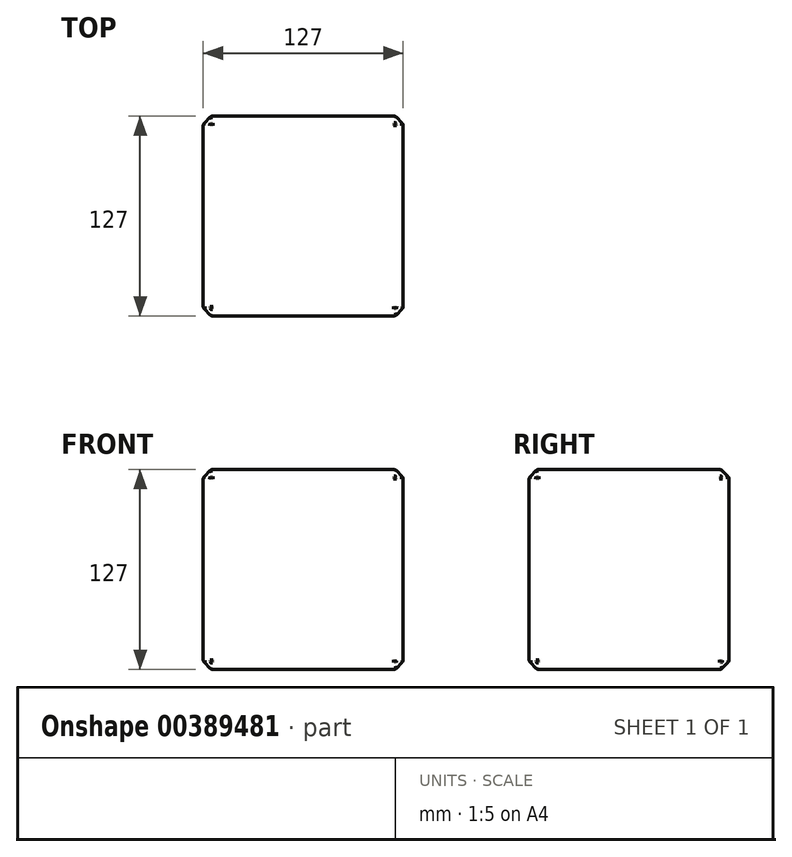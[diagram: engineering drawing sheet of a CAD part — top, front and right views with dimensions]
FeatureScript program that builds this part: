
annotation { "Feature Type Name" : "Feature", "Feature Type Description" : "" }
export const myFeature = defineFeature(function(context is Context, id is Id, definition is map)
    precondition{}
    {
        {
            var Q0;
            Q0=qCreatedBy(makeId("Top.planeOp"),FACE);
            var sketch = newSketch(context, id + "F0", { "sketchPlane" : qUnion([Q0])});
            skLineSegment(sketch, "E0.bottom", {"start": v(63.5, 63.5) * mm, "end": v(-63.5, 63.5) * mm});
            skLineSegment(sketch, "E0.top", {"start": v(63.5, -63.5) * mm, "end": v(-63.5, -63.5) * mm});
            skLineSegment(sketch, "E0.left", {"start": v(63.5, 63.5) * mm, "end": v(63.5, -63.5) * mm});
            skLineSegment(sketch, "E0.right", {"start": v(-63.5, 63.5) * mm, "end": v(-63.5, -63.5) * mm});
            skPoint(sketch, "E0.middle", {"position": v(0, 0) * mm});
            skSolve(sketch);
        }
        {
            var Q0;
            Q0 = qSketchRegion(id + "F0", true);
            extrude(context, id + "F1", {"entities" : qUnion([Q0]), "depth" : 127 * mm});
        }
        {
            var Q0;
            Q0=makeQuery(id+"F1.opExtrude","CAP_EDGE",EDGE,{"disambiguationData":[OSD([sQuery(id+"F0.wireOp",EDGE,"E0.top")])],"isStart":false});
            var Q1;
            Q1=makeQuery(id+"F1.opExtrude","CAP_EDGE",EDGE,{"disambiguationData":[OSD([sQuery(id+"F0.wireOp",EDGE,"E0.left")])],"isStart":false});
            var Q2;
            Q2=makeQuery(id+"F1.opExtrude","SWEPT_EDGE",EDGE,{"disambiguationData":[OSD([sQuery(id+"F0.wireOp",EDGE,"E0.top"),sQuery(id+"F0.wireOp",EDGE,"E0.left")])]});
            var Q3;
            Q3=makeQuery(id+"F1.opExtrude","SWEPT_EDGE",EDGE,{"disambiguationData":[OSD([sQuery(id+"F0.wireOp",EDGE,"E0.bottom"),sQuery(id+"F0.wireOp",EDGE,"E0.left")])]});
            var Q4;
            Q4=makeQuery(id+"F1.opExtrude","CAP_EDGE",EDGE,{"disambiguationData":[OSD([sQuery(id+"F0.wireOp",EDGE,"E0.top")])],"isStart":true});
            var Q5;
            Q5=makeQuery(id+"F1.opExtrude","CAP_EDGE",EDGE,{"disambiguationData":[OSD([sQuery(id+"F0.wireOp",EDGE,"E0.left")])],"isStart":true});
            var Q6;
            Q6=makeQuery(id+"F1.opExtrude","SWEPT_EDGE",EDGE,{"disambiguationData":[OSD([sQuery(id+"F0.wireOp",EDGE,"E0.top"),sQuery(id+"F0.wireOp",EDGE,"E0.right")])]});
            var Q7;
            Q7=makeQuery(id+"F1.opExtrude","CAP_EDGE",EDGE,{"disambiguationData":[OSD([sQuery(id+"F0.wireOp",EDGE,"E0.right")])],"isStart":true});
            var Q8;
            Q8=makeQuery(id+"F1.opExtrude","CAP_EDGE",EDGE,{"disambiguationData":[OSD([sQuery(id+"F0.wireOp",EDGE,"E0.right")])],"isStart":false});
            var Q9;
            Q9=makeQuery(id+"F1.opExtrude","SWEPT_FACE",FACE,{"disambiguationData":[OSD([sQuery(id+"F0.wireOp",EDGE,"E0.bottom")])]});
            chamfer(context, id + "F2", {"entities" : qUnion([Q0, Q1, Q2, Q3, Q4, Q5, Q6, Q7, Q8, Q9]), "width" : 5.08 * mm, "tangentPropagation" : true});
        }
        {
            var Q0;
            {var subQ0=sQuery(id+"F0.wireOp",EDGE,"E0.top");Q0=makeQuery(id+"F2.opChamfer","BLEND_EDGE",EDGE,{"blendedFrom":[makeQuery(id+"F1.opExtrude","SWEPT_EDGE",EDGE,{"disambiguationData":[OSD([subQ0,sQuery(id+"F0.wireOp",EDGE,"E0.left")])]}),makeQuery(id+"F1.opExtrude","SWEPT_FACE",FACE,{"disambiguationData":[OSD([subQ0])]})],"blendedInto":[makeQuery(id+"F1.opExtrude","SWEPT_FACE",FACE,{"disambiguationData":[OSD([subQ0])]})]});}
            var Q1;
            {var subQ0=sQuery(id+"F0.wireOp",EDGE,"E0.left");Q1=makeQuery(id+"F2.opChamfer","BLEND_EDGE",EDGE,{"blendedFrom":[makeQuery(id+"F1.opExtrude","SWEPT_EDGE",EDGE,{"disambiguationData":[OSD([sQuery(id+"F0.wireOp",EDGE,"E0.top"),subQ0])]}),makeQuery(id+"F1.opExtrude","SWEPT_FACE",FACE,{"disambiguationData":[OSD([subQ0])]})],"blendedInto":[makeQuery(id+"F1.opExtrude","SWEPT_FACE",FACE,{"disambiguationData":[OSD([subQ0])]})]});}
            var Q2;
            {var subQ0=sQuery(id+"F0.wireOp",EDGE,"E0.left");var subQ1=sQuery(id+"F0.wireOp",EDGE,"E0.top");Q2=makeQuery(id+"F2.opChamfer","BLEND_EDGE",EDGE,{"blendedFrom":[makeQuery(id+"F1.opExtrude","CAP_VERTEX",VERTEX,{"disambiguationData":[OSD([subQ1,subQ0])],"isStart":false}),makeQuery(id+"F1.opExtrude","SWEPT_EDGE",EDGE,{"disambiguationData":[OSD([subQ1,subQ0])]})],"blendedInto":[]});}
            var Q3;
            {var subQ0=sQuery(id+"F0.wireOp",EDGE,"E0.left");Q3=makeQuery(id+"F2.opChamfer","BLEND_EDGE",EDGE,{"blendedFrom":[makeQuery(id+"F1.opExtrude","CAP_EDGE",EDGE,{"disambiguationData":[OSD([subQ0])],"isStart":false}),makeQuery(id+"F1.opExtrude","SWEPT_FACE",FACE,{"disambiguationData":[OSD([subQ0])]})],"blendedInto":[makeQuery(id+"F1.opExtrude","SWEPT_FACE",FACE,{"disambiguationData":[OSD([subQ0])]})]});}
            var Q4;
            {var subQ0=sQuery(id+"F0.wireOp",EDGE,"E0.left");Q4=makeQuery(id+"F2.opChamfer","BLEND_EDGE",EDGE,{"blendedFrom":[makeQuery(id+"F1.opExtrude","CAP_EDGE",EDGE,{"disambiguationData":[OSD([subQ0])],"isStart":false}),makeQuery(id+"F1.opExtrude","CAP_FACE",FACE,{"disambiguationData":[OSD([sQuery(id+"F0.wireOp",EDGE,"E0.bottom"),sQuery(id+"F0.wireOp",EDGE,"E0.top"),subQ0,sQuery(id+"F0.wireOp",EDGE,"E0.right")])],"isStart":false})],"blendedInto":[makeQuery(id+"F1.opExtrude","CAP_FACE",FACE,{"disambiguationData":[OSD([sQuery(id+"F0.wireOp",EDGE,"E0.bottom"),sQuery(id+"F0.wireOp",EDGE,"E0.top"),subQ0,sQuery(id+"F0.wireOp",EDGE,"E0.right")])],"isStart":false})]});}
            var Q5;
            {var subQ0=sQuery(id+"F0.wireOp",EDGE,"E0.left");Q5=makeQuery(id+"F2.opChamfer","BLEND_EDGE",EDGE,{"blendedFrom":[makeQuery(id+"F1.opExtrude","CAP_VERTEX",VERTEX,{"disambiguationData":[OSD([sQuery(id+"F0.wireOp",EDGE,"E0.top"),subQ0])],"isStart":false}),makeQuery(id+"F1.opExtrude","CAP_EDGE",EDGE,{"disambiguationData":[OSD([subQ0])],"isStart":false})],"blendedInto":[]});}
            var Q6;
            {var subQ0=sQuery(id+"F0.wireOp",EDGE,"E0.top");Q6=makeQuery(id+"F2.opChamfer","BLEND_EDGE",EDGE,{"blendedFrom":[makeQuery(id+"F1.opExtrude","CAP_EDGE",EDGE,{"disambiguationData":[OSD([subQ0])],"isStart":false}),makeQuery(id+"F1.opExtrude","CAP_FACE",FACE,{"disambiguationData":[OSD([sQuery(id+"F0.wireOp",EDGE,"E0.bottom"),subQ0,sQuery(id+"F0.wireOp",EDGE,"E0.left"),sQuery(id+"F0.wireOp",EDGE,"E0.right")])],"isStart":false})],"blendedInto":[makeQuery(id+"F1.opExtrude","CAP_FACE",FACE,{"disambiguationData":[OSD([sQuery(id+"F0.wireOp",EDGE,"E0.bottom"),subQ0,sQuery(id+"F0.wireOp",EDGE,"E0.left"),sQuery(id+"F0.wireOp",EDGE,"E0.right")])],"isStart":false})]});}
            var Q7;
            {var subQ0=sQuery(id+"F0.wireOp",EDGE,"E0.top");Q7=makeQuery(id+"F2.opChamfer","BLEND_EDGE",EDGE,{"blendedFrom":[makeQuery(id+"F1.opExtrude","CAP_EDGE",EDGE,{"disambiguationData":[OSD([subQ0])],"isStart":false}),makeQuery(id+"F1.opExtrude","SWEPT_FACE",FACE,{"disambiguationData":[OSD([subQ0])]})],"blendedInto":[makeQuery(id+"F1.opExtrude","SWEPT_FACE",FACE,{"disambiguationData":[OSD([subQ0])]})]});}
            var Q8;
            {var subQ0=sQuery(id+"F0.wireOp",EDGE,"E0.top");Q8=makeQuery(id+"F2.opChamfer","BLEND_EDGE",EDGE,{"blendedFrom":[makeQuery(id+"F1.opExtrude","CAP_VERTEX",VERTEX,{"disambiguationData":[OSD([subQ0,sQuery(id+"F0.wireOp",EDGE,"E0.left")])],"isStart":false}),makeQuery(id+"F1.opExtrude","CAP_EDGE",EDGE,{"disambiguationData":[OSD([subQ0])],"isStart":false})],"blendedInto":[]});}
            var Q9;
            {var subQ0=sQuery(id+"F0.wireOp",EDGE,"E0.top");Q9=makeQuery(id+"F2.opChamfer","BLEND_EDGE",EDGE,{"blendedFrom":[makeQuery(id+"F1.opExtrude","CAP_VERTEX",VERTEX,{"disambiguationData":[OSD([subQ0,sQuery(id+"F0.wireOp",EDGE,"E0.right")])],"isStart":false}),makeQuery(id+"F1.opExtrude","CAP_EDGE",EDGE,{"disambiguationData":[OSD([subQ0])],"isStart":false})],"blendedInto":[]});}
            var Q10;
            {var subQ0=sQuery(id+"F0.wireOp",EDGE,"E0.right");var subQ1=sQuery(id+"F0.wireOp",EDGE,"E0.top");Q10=makeQuery(id+"F2.opChamfer","BLEND_FACE",FACE,{"disambiguationData":[OSD([subQ1,subQ0]),TDD([makeQuery(id+"F1.opExtrude","SWEPT_EDGE",EDGE,{"disambiguationData":[OSD([subQ1,subQ0])]})])]});}
            var Q11;
            {var subQ0=sQuery(id+"F0.wireOp",EDGE,"E0.right");Q11=makeQuery(id+"F2.opChamfer","BLEND_FACE",FACE,{"disambiguationData":[OSD([subQ0]),TDD([makeQuery(id+"F1.opExtrude","CAP_EDGE",EDGE,{"disambiguationData":[OSD([subQ0])],"isStart":false})])]});}
            var Q12;
            {var subQ0=sQuery(id+"F0.wireOp",EDGE,"E0.top");Q12=makeQuery(id+"F2.opChamfer","BLEND_FACE",FACE,{"disambiguationData":[OSD([subQ0]),TDD([makeQuery(id+"F1.opExtrude","CAP_EDGE",EDGE,{"disambiguationData":[OSD([subQ0])],"isStart":true})])]});}
            var Q13;
            {var subQ0=sQuery(id+"F0.wireOp",EDGE,"E0.right");Q13=makeQuery(id+"F2.opChamfer","BLEND_FACE",FACE,{"disambiguationData":[OSD([subQ0]),TDD([makeQuery(id+"F1.opExtrude","CAP_EDGE",EDGE,{"disambiguationData":[OSD([subQ0])],"isStart":true})])]});}
            var Q14;
            {var subQ0=sQuery(id+"F0.wireOp",EDGE,"E0.left");Q14=makeQuery(id+"F2.opChamfer","BLEND_FACE",FACE,{"disambiguationData":[OSD([subQ0]),TDD([makeQuery(id+"F1.opExtrude","CAP_EDGE",EDGE,{"disambiguationData":[OSD([subQ0])],"isStart":true})])]});}
            var Q15;
            {var subQ0=sQuery(id+"F0.wireOp",EDGE,"E0.bottom");Q15=makeQuery(id+"F2.opChamfer","BLEND_FACE",FACE,{"disambiguationData":[OSD([subQ0]),TDD([makeQuery(id+"F1.opExtrude","CAP_EDGE",EDGE,{"disambiguationData":[OSD([subQ0])],"isStart":true})])]});}
            var Q16;
            {var subQ0=sQuery(id+"F0.wireOp",EDGE,"E0.left");var subQ1=sQuery(id+"F0.wireOp",EDGE,"E0.bottom");Q16=makeQuery(id+"F2.opChamfer","BLEND_FACE",FACE,{"disambiguationData":[OSD([subQ1,subQ0]),TDD([makeQuery(id+"F1.opExtrude","SWEPT_EDGE",EDGE,{"disambiguationData":[OSD([subQ1,subQ0])]})])]});}
            var Q17;
            {var subQ0=sQuery(id+"F0.wireOp",EDGE,"E0.bottom");Q17=makeQuery(id+"F2.opChamfer","BLEND_FACE",FACE,{"disambiguationData":[OSD([subQ0]),TDD([makeQuery(id+"F1.opExtrude","CAP_EDGE",EDGE,{"disambiguationData":[OSD([subQ0])],"isStart":false})])]});}
            var Q18;
            {var subQ0=sQuery(id+"F0.wireOp",EDGE,"E0.right");var subQ1=sQuery(id+"F0.wireOp",EDGE,"E0.bottom");Q18=makeQuery(id+"F2.opChamfer","BLEND_FACE",FACE,{"disambiguationData":[OSD([subQ1,subQ0]),TDD([makeQuery(id+"F1.opExtrude","SWEPT_EDGE",EDGE,{"disambiguationData":[OSD([subQ1,subQ0])]})])]});}
            var Q19;
            {var subQ0=sQuery(id+"F0.wireOp",EDGE,"E0.left");Q19=makeQuery(id+"F2.opChamfer","BLEND_EDGE",EDGE,{"blendedFrom":[makeQuery(id+"F1.opExtrude","CAP_VERTEX",VERTEX,{"disambiguationData":[OSD([sQuery(id+"F0.wireOp",EDGE,"E0.bottom"),subQ0])],"isStart":false}),makeQuery(id+"F1.opExtrude","CAP_EDGE",EDGE,{"disambiguationData":[OSD([subQ0])],"isStart":false})],"blendedInto":[]});}
            var Q20;
            {var subQ0=sQuery(id+"F0.wireOp",EDGE,"E0.left");var subQ1=sQuery(id+"F0.wireOp",EDGE,"E0.top");Q20=makeQuery(id+"F2.opChamfer","BLEND_EDGE",EDGE,{"blendedFrom":[makeQuery(id+"F1.opExtrude","CAP_VERTEX",VERTEX,{"disambiguationData":[OSD([subQ1,subQ0])],"isStart":true}),makeQuery(id+"F1.opExtrude","SWEPT_EDGE",EDGE,{"disambiguationData":[OSD([subQ1,subQ0])]})],"blendedInto":[]});}
            fillet(context, id + "F3", {"entities" : qUnion([Q0, Q1, Q2, Q3, Q4, Q5, Q6, Q7, Q8, Q9, Q10, Q11, Q12, Q13, Q14, Q15, Q16, Q17, Q18, Q19, Q20]), "radius" : 2.54 * mm, "tangentPropagation" : true, "allowEdgeOverflow" : false});
        }
    });
